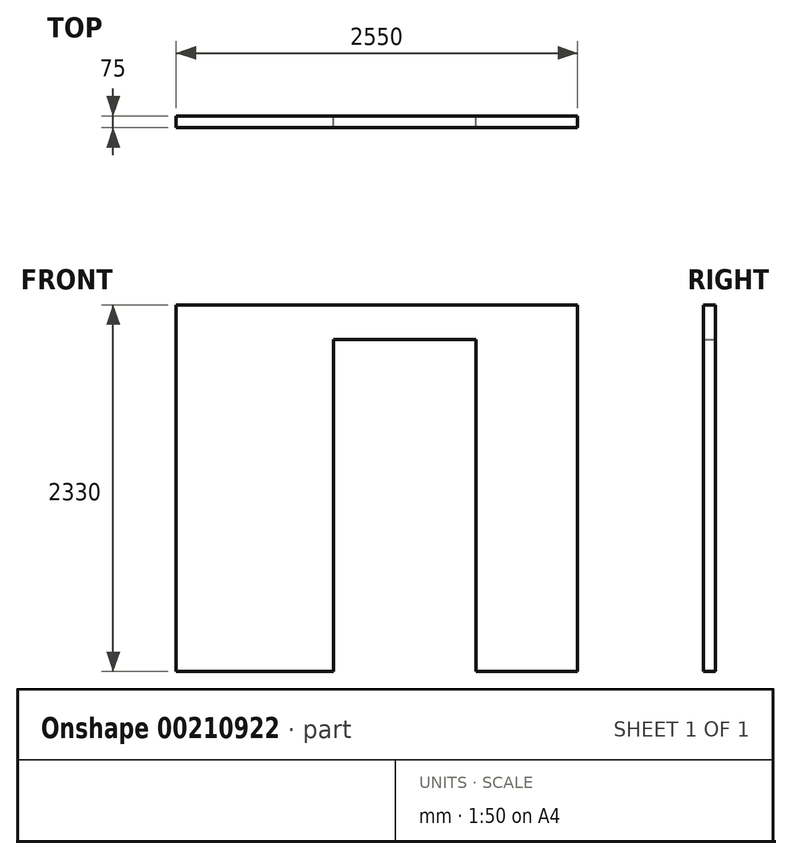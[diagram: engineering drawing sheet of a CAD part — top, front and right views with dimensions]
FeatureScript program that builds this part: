
annotation { "Feature Type Name" : "Feature", "Feature Type Description" : "" }
export const myFeature = defineFeature(function(context is Context, id is Id, definition is map)
    precondition{}
    {
        {
            var Q0;
            Q0=qCreatedBy(makeId("Front.planeOp"),FACE);
            var sketch = newSketch(context, id + "F0", { "sketchPlane" : qUnion([Q0])});
            skLineSegment(sketch, "E0.bottom", {"start": v(0, 0) * mm, "end": v(2550, 0) * mm});
            skLineSegment(sketch, "E0.right", {"start": v(2550, 0) * mm, "end": v(2550, 2330) * mm});
            skLineSegment(sketch, "E1", {"start": v(0, 2330) * mm, "end": v(2550, 2330) * mm});
            skLineSegment(sketch, "E2", {"start": v(0, 0) * mm, "end": v(0, 2330) * mm});
            skLineSegment(sketch, "E3.bottom", {"start": v(1000, 0) * mm, "end": v(1905, 0) * mm});
            skLineSegment(sketch, "E3.top", {"start": v(1000, 2110) * mm, "end": v(1905, 2110) * mm});
            skLineSegment(sketch, "E3.left", {"start": v(1000, 0) * mm, "end": v(1000, 2110) * mm});
            skLineSegment(sketch, "E3.right", {"start": v(1905, 0) * mm, "end": v(1905, 2110) * mm});
            skSolve(sketch);
        }
        {
            var Q0;
            Q0=makeQuery(id+"F0.imprint","IMPRINT",FACE,{"disambiguationData":[TD([[makeQuery(id+"F0.imprint","IMPRINT",EDGE,{"derivedFrom":sQuery(id+"F0.wireOp",EDGE,"E0.bottom")}),1.0]])]});
            extrude(context, id + "F1", {"entities" : qUnion([Q0]), "depth" : 75 * mm});
        }
    });
